# Revit family: FS730
name_source: partatom
category: Plumbing Fixtures
revit_build: Autodesk Revit 2018 (Build: 20170223_1515(x64)
units: mm (PartAtom-declared; Revit-internal decimal feet)

## family parameters
Cut with Voids When Loaded = No
Host = Face
Part Type = Normal
Room Calculation Point = No
Round Connector Dimension = Use Radius
Shared = No

## types (9) — shared parameters
Default Elevation = 0' - 0"
Description = 12” x 12” 8” FLOOR AREA AND INDIRECT SANITARY WASTE DRAIN
Floor Drain Material = Paint - Sherwin Williams Paint - #952C2A - Bellwood Red
Manufacturer = MIFAB
Model = FS730
URL = WWW.MIFAB.COM
zero-valued in all types: CWFU, WFU

## per-type parameters (varying)
| type | Body Height | Pipe Diameter | Pipe Radius |
| PIPE SIZE_2" NO HUB (STANDARD) 9 3/4" | 0' - 9 3/4" | 0' - 2" | 0' - 1" |
| PIPE SIZE_3" NO HUB (STANDARD) 9 3/4" | 0' - 9 3/4" | 0' - 3" | 0' - 1 1/2" |
| PIPE SIZE_4" NO HUB (STANDARD) 10 1/2" | 0' - 10 1/2" | 0' - 4" | 0' - 2" |
| PIPE SIZE_2" PUSH ON (P) 10 7/8” | 0' - 10 7/8" | 0' - 2" | 0' - 1" |
| PIPE SIZE_3" PUSH ON (P) 9 3/4” | 0' - 9 3/4" | 0' - 3" | 0' - 1 1/2" |
| PIPE SIZE_4" PUSH ON (P) 10 7/8” | 0' - 10 7/8" | 0' - 4" | 0' - 2" |
| PIPE SIZE_2" INSIDE CAULK (X) 12" | 1' - 0" | 0' - 2" | 0' - 1" |
| PIPE SIZE_3" INSIDE CAULK (X) 12" | 1' - 0" | 0' - 3" | 0' - 1 1/2" |
| PIPE SIZE_4" INSIDE CAULK (X) 10 5/8" | 0' - 10 5/8" | 0' - 3" | 0' - 1 1/2" |

## geometry (parser evidence)
native form markers: Blend x2, Sweep x6
no freeform markers — native parametric forms only
